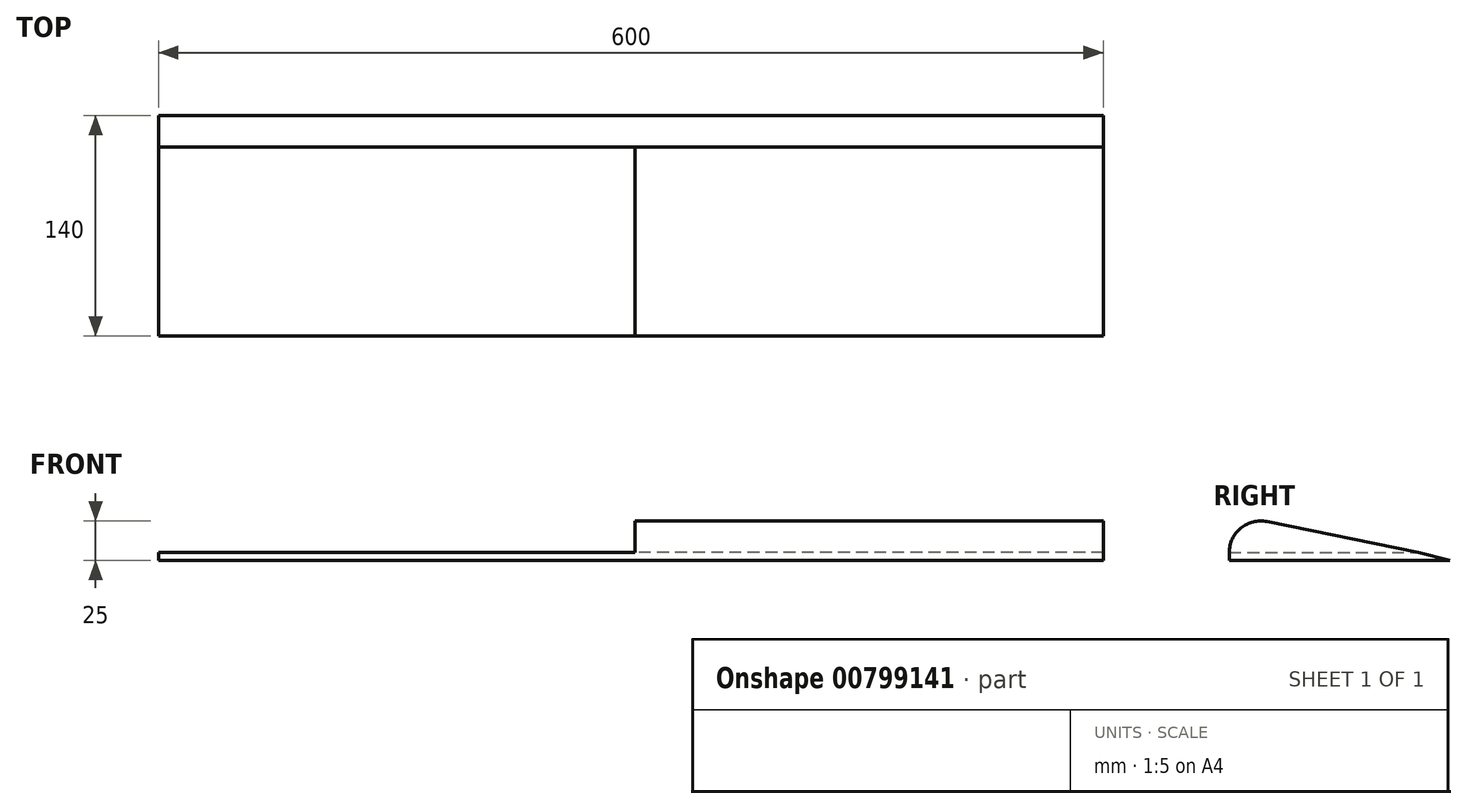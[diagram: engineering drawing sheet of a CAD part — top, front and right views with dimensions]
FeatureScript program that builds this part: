
annotation { "Feature Type Name" : "Feature", "Feature Type Description" : "" }
export const myFeature = defineFeature(function(context is Context, id is Id, definition is map)
    precondition{}
    {
        {
            var Q0;
            Q0=qCreatedBy(makeId("Top.planeOp"),FACE);
            var sketch = newSketch(context, id + "F0", { "sketchPlane" : qUnion([Q0])});
            skLineSegment(sketch, "E0", {"start": v(0, 0) * mm, "end": v(-300, 0) * mm});
            skLineSegment(sketch, "E1", {"start": v(-300, 0) * mm, "end": v(-300, 140) * mm});
            skLineSegment(sketch, "E2", {"start": v(-300, 140) * mm, "end": v(300, 140) * mm});
            skLineSegment(sketch, "E3", {"start": v(300, 140) * mm, "end": v(300, 0) * mm});
            skLineSegment(sketch, "E4", {"start": v(300, 0) * mm, "end": v(0, 0) * mm});
            skSolve(sketch);
        }
        {
            var Q0;
            Q0=qCreatedBy(makeId("Right.planeOp"),FACE);
            cPlane(context, id + "F1", {"entities" : qUnion([Q0]), "cplaneType" : CPlaneType.OFFSET, "offset" : 2.5 * mm, "width" : 150 * mm, "height" : 150 * mm});
        }
        {
            var Q0;
            Q0=qCreatedBy(makeId("Right.planeOp"),FACE);
            cPlane(context, id + "F2", {"entities" : qUnion([Q0]), "cplaneType" : CPlaneType.OFFSET, "offset" : 2.5 * mm, "oppositeDirection" : true, "width" : 150 * mm, "height" : 150 * mm});
        }
        {
            var Q0;
            Q0 = qSketchRegion(id + "F0", true);
            extrude(context, id + "F3", {"entities" : qUnion([Q0]), "endBound" : BoundingType.SYMMETRIC, "depth" : 5 * mm, "offsetDistance" : 25 * mm});
        }
        {
            var Q0;
            Q0=qCreatedBy(id+"F1.planeOp",FACE);
            var sketch = newSketch(context, id + "F4", { "sketchPlane" : qUnion([Q0])});
            skLineSegment(sketch, "E5", {"start": v(0, 0) * mm, "end": v(0, 2.5) * mm});
            skLineSegment(sketch, "E6", {"start": v(0, 0) * mm, "end": v(0, -2.5) * mm});
            skLineSegment(sketch, "E7", {"start": v(0, 2.5) * mm, "end": v(140, 2.5) * mm});
            skLineSegment(sketch, "E8", {"start": v(140, 2.5) * mm, "end": v(140, -2.5) * mm});
            skLineSegment(sketch, "E9", {"start": v(140, -2.5) * mm, "end": v(0, -2.5) * mm});
            skArc(sketch, "E10", {"start": v(0, 2.5) * mm, "mid": v(7.35, 18) * mm, "end": v(24, 22.1) * mm});
            skLineSegment(sketch, "E11", {"start": v(140, -2.5) * mm, "end": v(120, 2.5) * mm});
            skLineSegment(sketch, "E12", {"start": v(24, 22.1) * mm, "end": v(120, 2.5) * mm});
            skSolve(sketch);
        }
        {
            var Q0;
            Q0 = qSketchRegion(id + "F4", true);
            extrude(context, id + "F5", {"entities" : qUnion([Q0]), "operationType" : NewBodyOperationType.ADD, "depth" : 297.5 * mm, "offsetDistance" : 25 * mm});
        }
        {
            var Q0;
            Q0=makeQuery(id+"F3.opExtrude","SWEPT_FACE",FACE,{"disambiguationData":[OSD([sQuery(id+"F0.wireOp",EDGE,"E1")])]});
            cPlane(context, id + "F6", {"entities" : qUnion([Q0]), "cplaneType" : CPlaneType.OFFSET, "offset" : 0 * mm, "width" : 150 * mm, "height" : 150 * mm});
        }
        {
            var Q0;
            Q0=qCreatedBy(id+"F6.planeOp",FACE);
            var sketch = newSketch(context, id + "F7", { "sketchPlane" : qUnion([Q0])});
            skLineSegment(sketch, "E13", {"start": v(0, 0) * mm, "end": v(0, 2.5) * mm});
            skLineSegment(sketch, "E14", {"start": v(0, 0) * mm, "end": v(0, -2.5) * mm});
            skLineSegment(sketch, "E15", {"start": v(0, -2.5) * mm, "end": v(-140, -2.5) * mm});
            skLineSegment(sketch, "E16", {"start": v(0, 2.5) * mm, "end": v(-120, 2.5) * mm});
            skLineSegment(sketch, "E17", {"start": v(-120, 2.5) * mm, "end": v(-140, -2.5) * mm});
            skLineSegment(sketch, "E18", {"start": v(-120, 2.5) * mm, "end": v(-140, 2.5) * mm});
            skLineSegment(sketch, "E19", {"start": v(-140, 2.5) * mm, "end": v(-140, -2.5) * mm});
            skSolve(sketch);
        }
        {
            var Q0;
            Q0=makeQuery(id+"F7.imprint","IMPRINT",FACE,{"disambiguationData":[TD([[makeQuery(id+"F7.imprint","IMPRINT",EDGE,{"derivedFrom":sQuery(id+"F7.wireOp",EDGE,"E17")}),-1.0]])]});
            extrude(context, id + "F8", {"entities" : qUnion([Q0]), "operationType" : NewBodyOperationType.REMOVE, "oppositeDirection" : true, "depth" : 600 * mm, "offsetDistance" : 25 * mm});
        }
        {
            var Q0;
            Q0=qCreatedBy(id+"F2.planeOp",FACE);
            var sketch = newSketch(context, id + "F9", { "sketchPlane" : qUnion([Q0])});
            skLineSegment(sketch, "E20", {"start": v(0, 0) * mm, "end": v(0, 2.5) * mm});
            skLineSegment(sketch, "E21", {"start": v(0, 0) * mm, "end": v(0, -2.5) * mm});
            skLineSegment(sketch, "E22", {"start": v(0, 2.5) * mm, "end": v(140, 2.5) * mm});
            skLineSegment(sketch, "E23", {"start": v(140, 2.5) * mm, "end": v(140, -2.5) * mm});
            skLineSegment(sketch, "E24", {"start": v(140, -2.5) * mm, "end": v(0, -2.5) * mm});
            skArc(sketch, "E25", {"start": v(0, 2.5) * mm, "mid": v(7.35, 18) * mm, "end": v(24, 22.1) * mm});
            skPoint(sketch, "E26", {"position": v(120, 2.5) * mm});
            skLineSegment(sketch, "E27", {"start": v(24, 22.1) * mm, "end": v(120, 2.5) * mm});
            skLineSegment(sketch, "E28", {"start": v(120, 2.5) * mm, "end": v(140, -2.5) * mm});
            skSolve(sketch);
        }
        {
            var Q0;
            {var subQ0=sQuery(id+"F9.wireOp",EDGE,"E25");Q0=makeQuery(id+"F9.imprint","IMPRINT",FACE,{"disambiguationData":[TD([[makeQuery(id+"F9.imprint","IMPRINT",EDGE,{"derivedFrom":subQ0}),-1.0]])]});}
            var Q1;
            {var subQ1=sQuery(id+"F9.wireOp",EDGE,"E20");Q1=makeQuery(id+"F9.imprint","IMPRINT",FACE,{"disambiguationData":[TD([[makeQuery(id+"F9.imprint","IMPRINT",EDGE,{"derivedFrom":subQ1}),-1.0]])]});}
            extrude(context, id + "F10", {"entities" : qUnion([Q0, Q1]), "operationType" : NewBodyOperationType.ADD, "oppositeDirection" : true, "depth" : 297.5 * mm, "offsetDistance" : 25 * mm});
        }
    });
